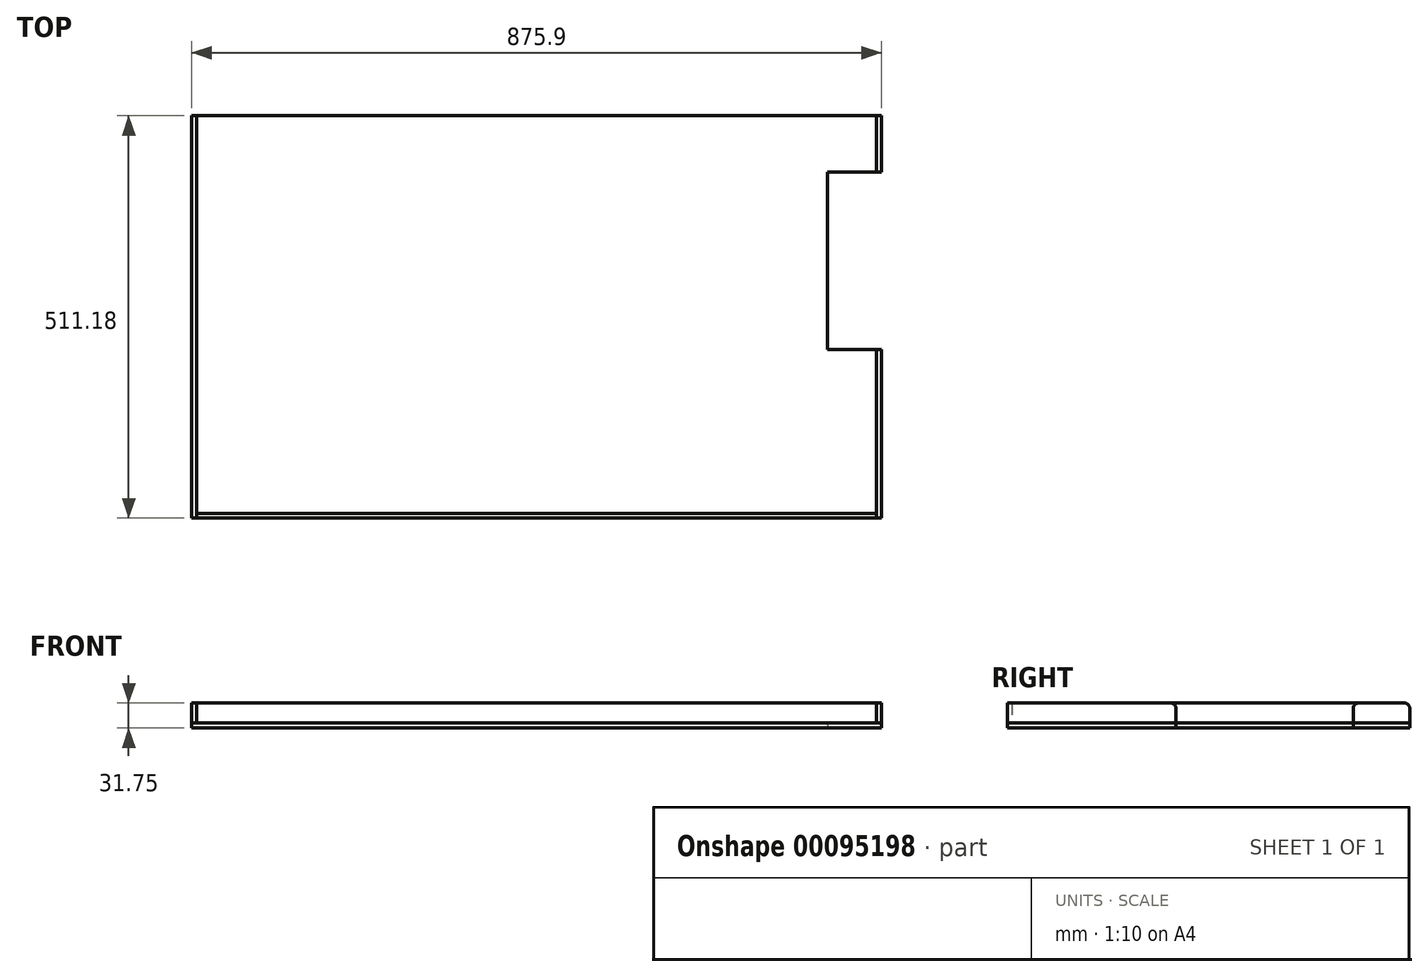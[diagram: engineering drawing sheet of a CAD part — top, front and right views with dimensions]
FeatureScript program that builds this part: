
annotation { "Feature Type Name" : "Feature", "Feature Type Description" : "" }
export const myFeature = defineFeature(function(context is Context, id is Id, definition is map)
    precondition{}
    {
        {
            var Q0;
            Q0=qCreatedBy(makeId("Top.planeOp"),FACE);
            var sketch = newSketch(context, id + "F0", { "sketchPlane" : qUnion([Q0])});
            skLineSegment(sketch, "E0.bottom", {"start": v(437.95, -255.59) * mm, "end": v(-437.95, -255.59) * mm});
            skLineSegment(sketch, "E0.top", {"start": v(437.95, 255.59) * mm, "end": v(-437.95, 255.59) * mm});
            skLineSegment(sketch, "E0.left", {"start": v(437.95, -255.59) * mm, "end": v(437.95, 271.46) * mm});
            skLineSegment(sketch, "E0.right", {"start": v(-437.95, -255.59) * mm, "end": v(-437.95, 255.59) * mm});
            skPoint(sketch, "E0.middle", {"position": v(0, 0) * mm});
            skLineSegment(sketch, "E1.bottom", {"start": v(437.95, 183.9) * mm, "end": v(369.88, 183.9) * mm});
            skLineSegment(sketch, "E1.top", {"start": v(437.95, -41.52) * mm, "end": v(369.88, -41.52) * mm});
            skLineSegment(sketch, "E1.left", {"start": v(437.95, 183.9) * mm, "end": v(437.95, -41.52) * mm});
            skLineSegment(sketch, "E1.right", {"start": v(369.88, 183.9) * mm, "end": v(369.88, -41.52) * mm});
            skLineSegment(sketch, "E2", {"start": v(437.95, 255.59) * mm, "end": v(437.95, 183.9) * mm, "construction": true});
            skSolve(sketch);
        }
        {
            var Q0;
            Q0=makeQuery(id+"F0.imprint","IMPRINT",FACE,{"disambiguationData":[TD([[makeQuery(id+"F0.imprint","IMPRINT",EDGE,{"derivedFrom":sQuery(id+"F0.wireOp",EDGE,"E0.bottom")}),-1.0]])]});
            extrude(context, id + "F1", {"entities" : qUnion([Q0]), "depth" : 6.35 * mm});
        }
        {
            var Q0;
            Q0=makeQuery(id+"F1.opExtrude","CAP_FACE",FACE,{"disambiguationData":[OSD([sQuery(id+"F0.wireOp",EDGE,"E0.bottom"),sQuery(id+"F0.wireOp",EDGE,"E0.top"),sQuery(id+"F0.wireOp",EDGE,"E0.left"),sQuery(id+"F0.wireOp",EDGE,"E0.right"),sQuery(id+"F0.wireOp",EDGE,"E1.bottom"),sQuery(id+"F0.wireOp",EDGE,"E1.top"),sQuery(id+"F0.wireOp",EDGE,"E1.right")])],"isStart":false});
            var sketch = newSketch(context, id + "F2", { "sketchPlane" : qUnion([Q0])});
            skLineSegment(sketch, "E3.0", {"start": v(431.96, -255.59) * mm, "end": v(431.96, -41.52) * mm});
            skLineSegment(sketch, "E3.1", {"start": v(431.96, 183.9) * mm, "end": v(431.96, 255.59) * mm});
            skLineSegment(sketch, "E3.3", {"start": v(-431.96, -255.59) * mm, "end": v(-431.96, 255.59) * mm});
            skLineSegment(sketch, "E3.4", {"start": v(431.96, -249.6) * mm, "end": v(-431.96, -249.6) * mm});
            skSolve(sketch);
        }
        {
            var Q0;
            {var subQ4=makeQuery(id+"F1.opExtrude","CAP_EDGE",EDGE,{"disambiguationData":[OSD([sQuery(id+"F0.wireOp",EDGE,"E0.right")])],"isStart":false});Q0=makeQuery(id+"F2.imprint","IMPRINT",FACE,{"disambiguationData":[TD([[makeQuery(id+"F2.imprint","IMPRINT",EDGE,{"derivedFrom":subQ4}),-1.0]])]});}
            extrude(context, id + "F3", {"entities" : qUnion([Q0]), "depth" : 25.4 * mm});
        }
        {
            var Q0;
            {var subQ0=sQuery(id+"F0.wireOp",EDGE,"E0.left");var subQ1=sQuery(id+"F0.wireOp",EDGE,"E0.bottom");var subQ3=makeQuery(id+"F1.opExtrude","CAP_EDGE",EDGE,{"disambiguationData":[OSD([subQ0]),TDD([makeQuery(id+"F0.imprint","IMPRINT",EDGE,{"disambiguationData":[TD([[makeQuery(id+"F0.imprint","INTERSECT",VERTEX,{"derivedFrom":[subQ1,subQ0]}),-1.0]])],"derivedFrom":subQ0})])],"isStart":false});Q0=makeQuery(id+"F2.imprint","IMPRINT",FACE,{"disambiguationData":[TD([[makeQuery(id+"F2.imprint","IMPRINT",EDGE,{"derivedFrom":subQ3}),1.0]])]});}
            extrude(context, id + "F4", {"entities" : qUnion([Q0]), "depth" : 25.4 * mm});
        }
        {
            var Q0;
            {var subQ3=sQuery(id+"F2.wireOp",EDGE,"E3.4");Q0=makeQuery(id+"F2.imprint","IMPRINT",FACE,{"disambiguationData":[TD([[makeQuery(id+"F2.imprint","IMPRINT",EDGE,{"derivedFrom":subQ3}),1.0]])]});}
            extrude(context, id + "F5", {"entities" : qUnion([Q0]), "depth" : 25.4 * mm});
        }
        {
            var Q0;
            {var subQ0=sQuery(id+"F2.wireOp",EDGE,"E3.1");Q0=makeQuery(id+"F2.imprint","IMPRINT",FACE,{"disambiguationData":[TD([[makeQuery(id+"F2.imprint","IMPRINT",EDGE,{"derivedFrom":subQ0}),-1.0]])]});}
            extrude(context, id + "F6", {"entities" : qUnion([Q0]), "depth" : 25.4 * mm});
        }
        {
            var Q0;
            Q0=makeQuery(id+"F6.opExtrude","CAP_EDGE",EDGE,{"disambiguationData":[OSD([sQuery(id+"F0.wireOp",EDGE,"E1.bottom")])],"isStart":false});
            var Q1;
            Q1=makeQuery(id+"F6.opExtrude","CAP_EDGE",EDGE,{"disambiguationData":[OSD([sQuery(id+"F0.wireOp",EDGE,"E0.top")])],"isStart":false});
            var Q2;
            Q2=makeQuery(id+"F4.opExtrude","CAP_EDGE",EDGE,{"disambiguationData":[OSD([sQuery(id+"F0.wireOp",EDGE,"E1.top")])],"isStart":false});
            var Q3;
            Q3=makeQuery(id+"F3.opExtrude","CAP_EDGE",EDGE,{"disambiguationData":[OSD([sQuery(id+"F0.wireOp",EDGE,"E0.top")])],"isStart":false});
            fillet(context, id + "F7", {"entities" : qUnion([Q0, Q1, Q2, Q3]), "radius" : 6.35 * mm, "tangentPropagation" : true, "allowEdgeOverflow" : false});
        }
    });
